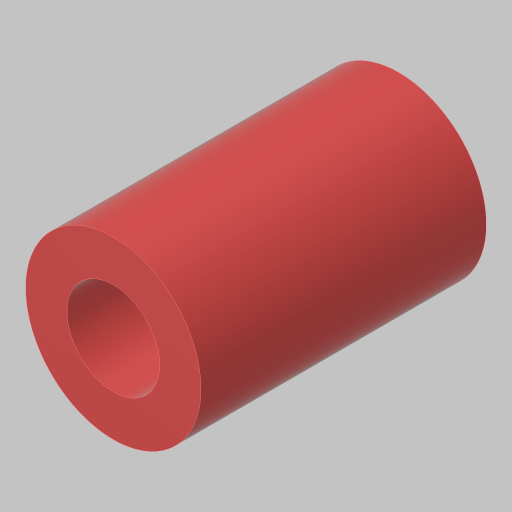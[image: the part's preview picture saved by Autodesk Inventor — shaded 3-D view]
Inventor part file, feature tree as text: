
AUTODESK INVENTOR PART (.ipt)
format: ipt  version: 2023.5 (Build 275446000, 446)  size: 114,176 bytes
history: native  units: in
note: dims shown in document units (in); Inventor stores cm internally (conversion verified against a paired STEP export)
features: extrude x1, sketch x1
ambient origin geometry x8: Origin, YZ Plane, XZ Plane, XY Plane, X Axis, Y Axis, Z Axis, Center Point
bodies: Solid1 (feature_tree)
feature tree (2):
  extrude  "Extrusion1"  Depth=1.725in
  sketch  "Sketch1"  dims[d0=0.56in d1=0.25in d2=1.725in d3=0.0in]
